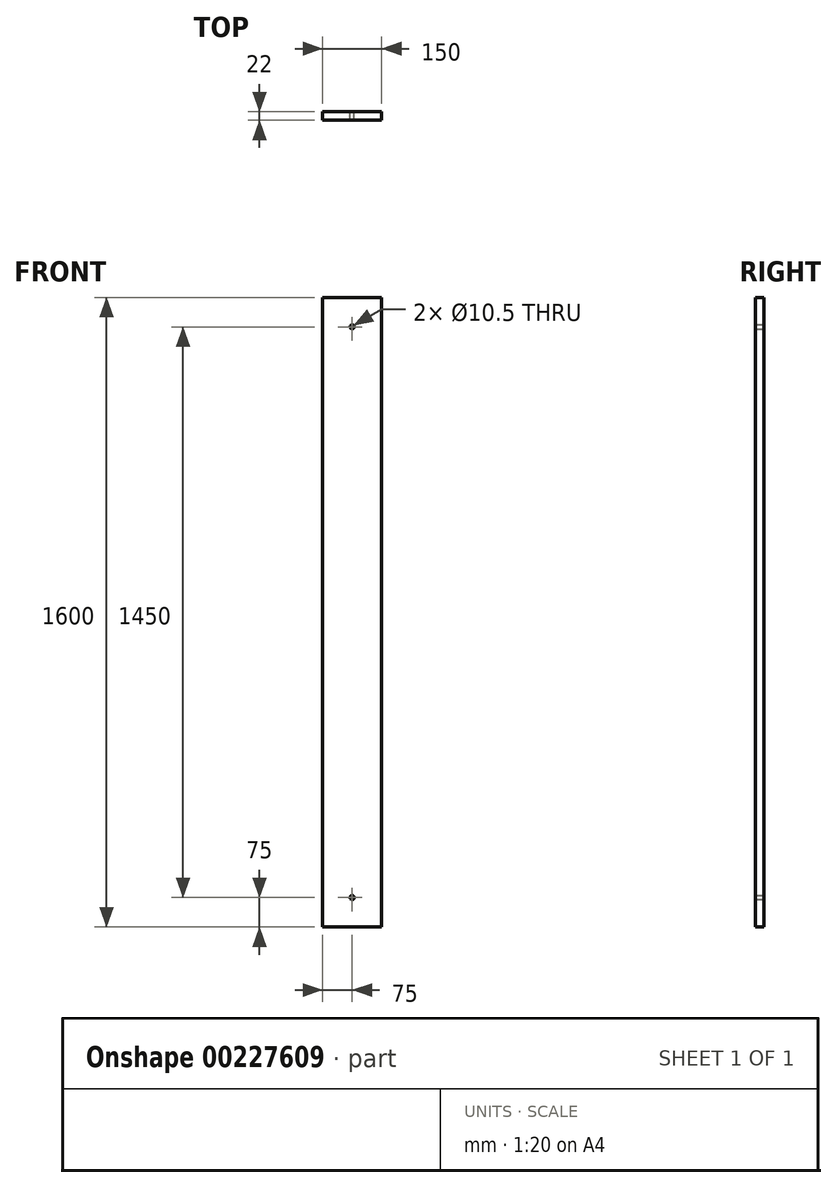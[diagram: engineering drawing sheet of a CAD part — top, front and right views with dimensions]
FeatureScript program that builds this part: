
annotation { "Feature Type Name" : "Feature", "Feature Type Description" : "" }
export const myFeature = defineFeature(function(context is Context, id is Id, definition is map)
    precondition{}
    {
        {
            var Q0;
            Q0=qCreatedBy(makeId("Front.planeOp"),FACE);
            var sketch = newSketch(context, id + "F0", { "sketchPlane" : qUnion([Q0])});
            skLineSegment(sketch, "E0.bottom", {"start": v(75, 800) * mm, "end": v(-75, 800) * mm});
            skLineSegment(sketch, "E0.top", {"start": v(75, -800) * mm, "end": v(-75, -800) * mm});
            skLineSegment(sketch, "E0.left", {"start": v(75, 800) * mm, "end": v(75, -800) * mm});
            skLineSegment(sketch, "E0.right", {"start": v(-75, 800) * mm, "end": v(-75, -800) * mm});
            skPoint(sketch, "E0.middle", {"position": v(0, 0) * mm});
            skLineSegment(sketch, "E1", {"start": v(0, 800) * mm, "end": v(0, -800) * mm, "construction": true});
            skLineSegment(sketch, "E2", {"start": v(-75, -725) * mm, "end": v(75, -725) * mm, "construction": true});
            skLineSegment(sketch, "E3", {"start": v(-75, 725) * mm, "end": v(75, 725) * mm, "construction": true});
            skCircle(sketch, "E4", {"center": v(0, -725) * mm, "radius": 5.25 * mm});
            skCircle(sketch, "E5", {"center": v(0, 725) * mm, "radius": 5.25 * mm});
            skSolve(sketch);
        }
        {
            var Q0;
            Q0=qSketchRegion(id+"F0",true);
            extrude(context, id + "F1", {"entities" : qUnion([Q0]), "depth" : 22 * mm});
        }
    });
